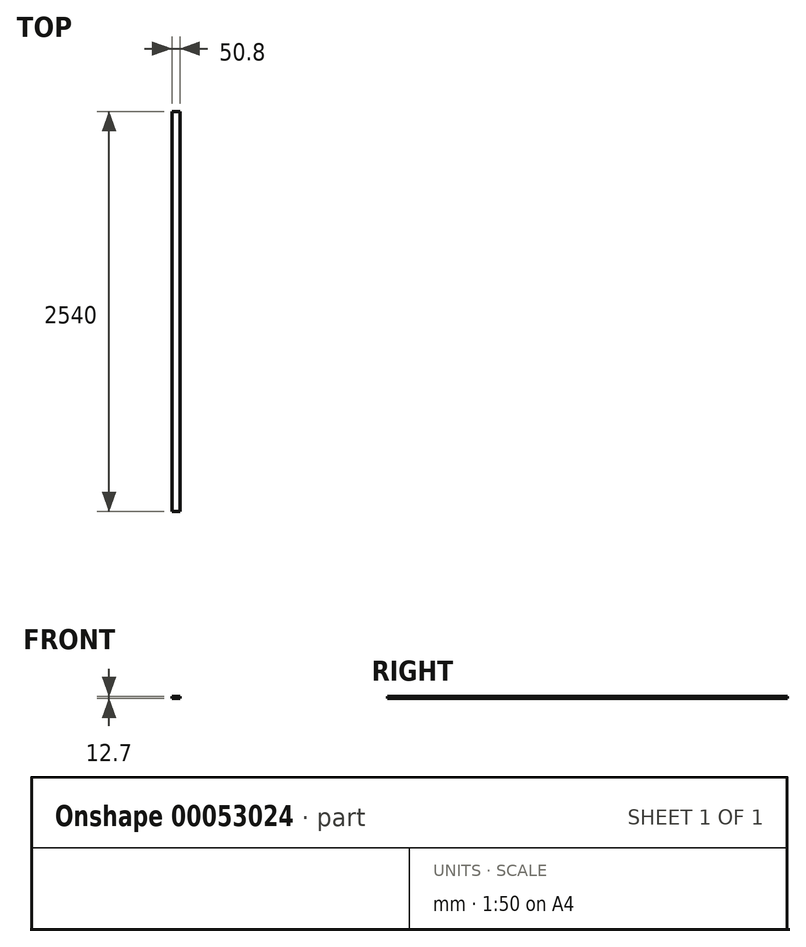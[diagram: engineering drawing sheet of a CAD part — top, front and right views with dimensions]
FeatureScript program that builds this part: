
annotation { "Feature Type Name" : "Feature", "Feature Type Description" : "" }
export const myFeature = defineFeature(function(context is Context, id is Id, definition is map)
    precondition{}
    {
        {
            var Q0;
            Q0=qCreatedBy(makeId("Front.planeOp"),FACE);
            var sketch = newSketch(context, id + "F0", { "sketchPlane" : qUnion([Q0])});
            skLineSegment(sketch, "E0.bottom", {"start": v(0, 0) * mm, "end": v(-50.8, 0) * mm});
            skLineSegment(sketch, "E0.top", {"start": v(0, 12.7) * mm, "end": v(-50.8, 12.7) * mm});
            skLineSegment(sketch, "E0.left", {"start": v(0, 0) * mm, "end": v(0, 12.7) * mm});
            skLineSegment(sketch, "E0.right", {"start": v(-50.8, 0) * mm, "end": v(-50.8, 12.7) * mm});
            skSolve(sketch);
        }
        {
            var Q0;
            Q0=makeQuery(id+"F0.imprint","IMPRINT",FACE,{"disambiguationData":[TD([[makeQuery(id+"F0.imprint","IMPRINT",EDGE,{"derivedFrom":sQuery(id+"F0.wireOp",EDGE,"E0.bottom")}),-1.0]])]});
            extrude(context, id + "F1", {"entities" : qUnion([Q0]), "depth" : 2540 * mm});
        }
    });
